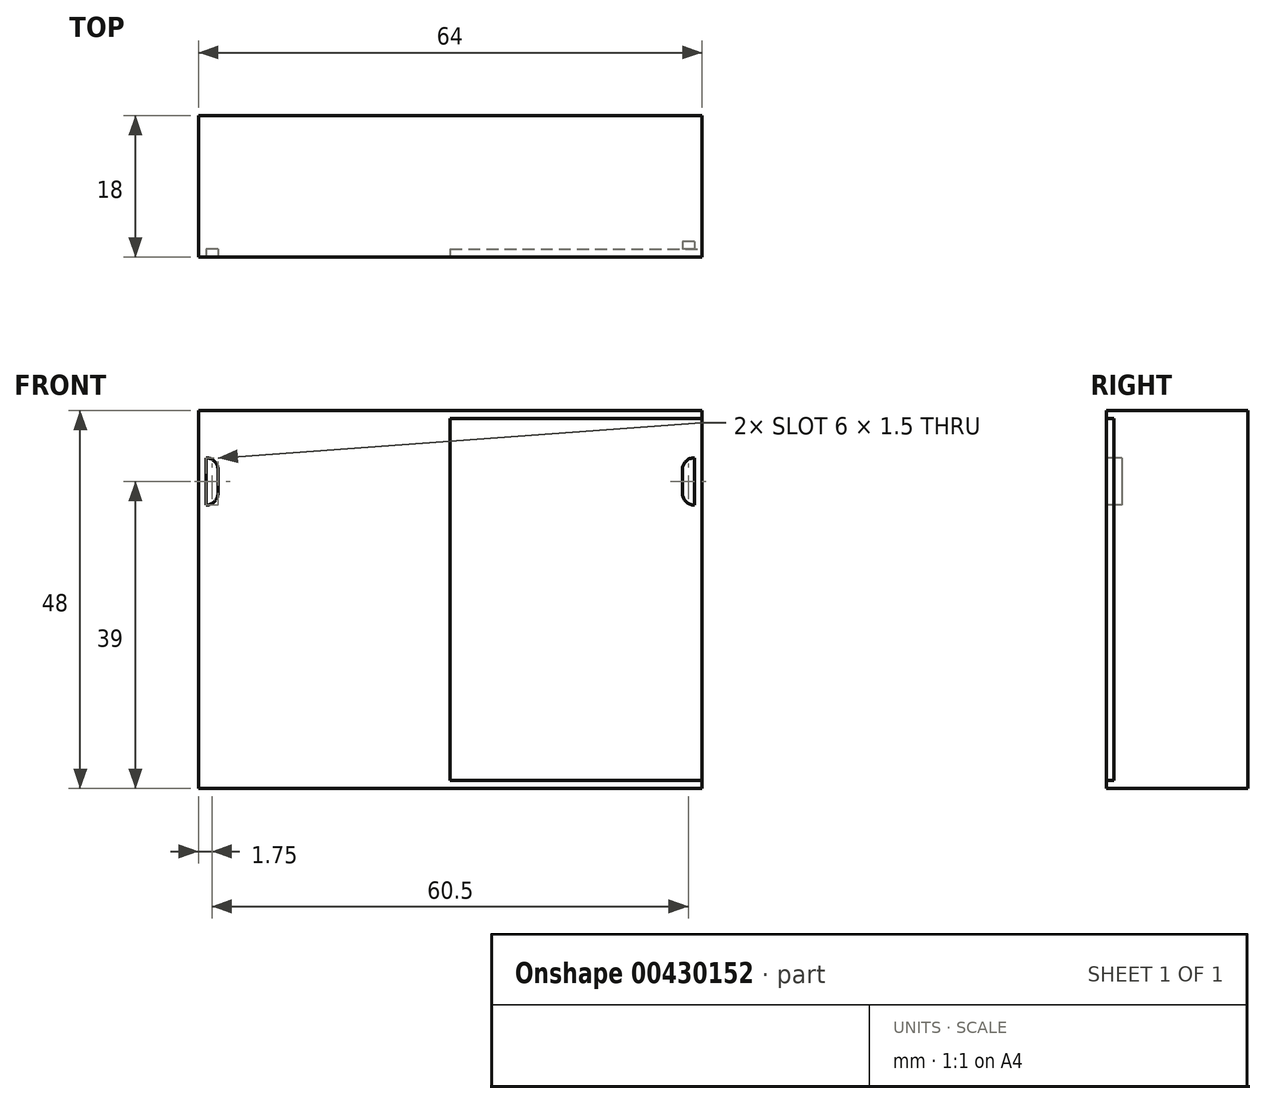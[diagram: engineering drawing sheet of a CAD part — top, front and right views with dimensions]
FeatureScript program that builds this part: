
annotation { "Feature Type Name" : "Feature", "Feature Type Description" : "" }
export const myFeature = defineFeature(function(context is Context, id is Id, definition is map)
    precondition{}
    {
        {
            var Q0;
            Q0=qCreatedBy(makeId("Top.planeOp"),FACE);
            var sketch = newSketch(context, id + "F0", { "sketchPlane" : qUnion([Q0])});
            skLineSegment(sketch, "E0.bottom", {"start": v(0, 0) * mm, "end": v(64, 0) * mm});
            skLineSegment(sketch, "E0.top", {"start": v(0, 18) * mm, "end": v(64, 18) * mm});
            skLineSegment(sketch, "E0.left", {"start": v(0, 0) * mm, "end": v(0, 18) * mm});
            skLineSegment(sketch, "E0.right", {"start": v(64, 0) * mm, "end": v(64, 18) * mm});
            skSolve(sketch);
        }
        {
            var Q0;
            Q0=makeQuery(id+"F0.imprint","IMPRINT",FACE,{"disambiguationData":[TD([[makeQuery(id+"F0.imprint","IMPRINT",EDGE,{"derivedFrom":sQuery(id+"F0.wireOp",EDGE,"E0.bottom")}),1.0]])]});
            extrude(context, id + "F1", {"entities" : qUnion([Q0]), "depth" : 48 * mm});
        }
        {
            var Q0;
            Q0=makeQuery(id+"F1.opExtrude","SWEPT_FACE",FACE,{"disambiguationData":[OSD([sQuery(id+"F0.wireOp",EDGE,"E0.bottom")])]});
            var sketch = newSketch(context, id + "F2", { "sketchPlane" : qUnion([Q0])});
            skLineSegment(sketch, "E1.bottom", {"start": v(32, 47) * mm, "end": v(64, 47) * mm});
            skLineSegment(sketch, "E1.top", {"start": v(32, 1) * mm, "end": v(64, 1) * mm});
            skLineSegment(sketch, "E1.left", {"start": v(32, 47) * mm, "end": v(32, 1) * mm});
            skLineSegment(sketch, "E1.right", {"start": v(64, 47) * mm, "end": v(64, 1) * mm});
            skSolve(sketch);
        }
        {
            var Q0;
            Q0=makeQuery(id+"F2.imprint","IMPRINT",FACE,{"disambiguationData":[TD([[makeQuery(id+"F2.imprint","IMPRINT",EDGE,{"derivedFrom":sQuery(id+"F2.wireOp",EDGE,"E1.bottom")}),-1.0]])]});
            extrude(context, id + "F3", {"entities" : qUnion([Q0]), "operationType" : NewBodyOperationType.REMOVE, "oppositeDirection" : true, "depth" : 1 * mm});
        }
        {
            var Q0;
            Q0=makeQuery(id+"F3.boolean.opBoolean","COPY",FACE,{"derivedFrom":makeQuery(id+"F3.opExtrude","CAP_FACE",FACE,{"disambiguationData":[OSD([sQuery(id+"F2.wireOp",EDGE,"E1.bottom"),sQuery(id+"F2.wireOp",EDGE,"E1.top"),sQuery(id+"F2.wireOp",EDGE,"E1.left"),sQuery(id+"F2.wireOp",EDGE,"E1.right")])],"isStart":false})});
            var sketch = newSketch(context, id + "F4", { "sketchPlane" : qUnion([Q0])});
            skLineSegment(sketch, "E2.bottom", {"start": v(63, 42) * mm, "end": v(63, 42) * mm});
            skLineSegment(sketch, "E2.top", {"start": v(63, 36) * mm, "end": v(63, 36) * mm});
            skLineSegment(sketch, "E2.left", {"start": v(61.5, 40.5) * mm, "end": v(61.5, 37.5) * mm});
            skLineSegment(sketch, "E3", {"start": v(63, 42) * mm, "end": v(63, 36) * mm});
            skPoint(sketch, "E4.visualSharp", {"position": v(61.5, 42) * mm});
            skArc(sketch, "E4.filletArc", {"start": v(63, 42) * mm, "mid": v(61.94, 41.56) * mm, "end": v(61.5, 40.5) * mm});
            skPoint(sketch, "E5.visualSharp", {"position": v(61.5, 36) * mm});
            skArc(sketch, "E5.filletArc", {"start": v(61.5, 37.5) * mm, "mid": v(61.94, 36.44) * mm, "end": v(63, 36) * mm});
            skSolve(sketch);
        }
        {
            var Q0;
            Q0=makeQuery(id+"F4.imprint","IMPRINT",FACE,{"disambiguationData":[TD([[makeQuery(id+"F4.imprint","IMPRINT",EDGE,{"derivedFrom":sQuery(id+"F4.wireOp",EDGE,"E2.left")}),1.0]])]});
            extrude(context, id + "F5", {"entities" : qUnion([Q0]), "operationType" : NewBodyOperationType.REMOVE, "oppositeDirection" : true, "depth" : 1 * mm});
        }
        {
            var Q0;
            Q0=makeQuery(id+"F1.opExtrude","SWEPT_FACE",FACE,{"disambiguationData":[OSD([sQuery(id+"F0.wireOp",EDGE,"E0.bottom")])]});
            var sketch = newSketch(context, id + "F6", { "sketchPlane" : qUnion([Q0])});
            skLineSegment(sketch, "E6.bottom", {"start": v(1, 42) * mm, "end": v(1, 42) * mm});
            skLineSegment(sketch, "E6.top", {"start": v(1, 36) * mm, "end": v(1, 36) * mm});
            skLineSegment(sketch, "E6.left", {"start": v(1, 42) * mm, "end": v(1, 36) * mm});
            skLineSegment(sketch, "E6.right", {"start": v(2.5, 40.5) * mm, "end": v(2.5, 37.5) * mm});
            skPoint(sketch, "E7.visualSharp", {"position": v(2.5, 42) * mm});
            skArc(sketch, "E7.filletArc", {"start": v(2.5, 40.5) * mm, "mid": v(2.06, 41.56) * mm, "end": v(1, 42) * mm});
            skPoint(sketch, "E8.visualSharp", {"position": v(2.5, 36) * mm});
            skArc(sketch, "E8.filletArc", {"start": v(1, 36) * mm, "mid": v(2.06, 36.44) * mm, "end": v(2.5, 37.5) * mm});
            skSolve(sketch);
        }
        {
            var Q0;
            Q0=makeQuery(id+"F6.imprint","IMPRINT",FACE,{"disambiguationData":[TD([[makeQuery(id+"F6.imprint","IMPRINT",EDGE,{"derivedFrom":sQuery(id+"F6.wireOp",EDGE,"E6.left")}),1.0]])]});
            extrude(context, id + "F7", {"entities" : qUnion([Q0]), "operationType" : NewBodyOperationType.REMOVE, "oppositeDirection" : true, "depth" : 1 * mm});
        }
    });
